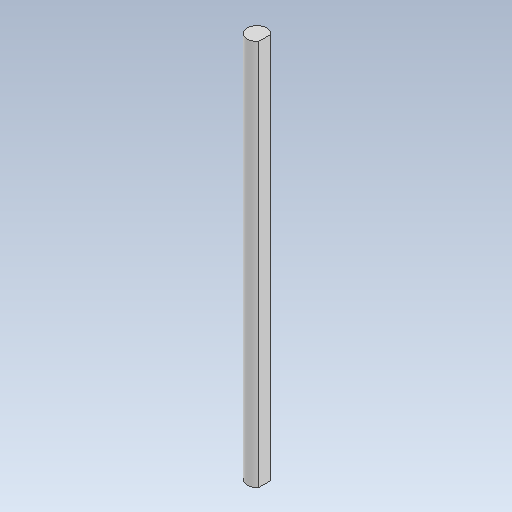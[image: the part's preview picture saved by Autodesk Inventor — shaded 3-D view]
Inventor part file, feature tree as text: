
AUTODESK INVENTOR PART (.ipt)
format: ipt  version: 2020 (Build 240168000, 168)  size: 74,240 bytes
history: native  units: in
note: dims shown in document units (in); Inventor stores cm internally (conversion verified against a paired STEP export)
features: other x3, sketch x1
ambient origin geometry x8: Origin, YZ Plane, XZ Plane, XY Plane, X Axis, Y Axis, Z Axis, Center Point
bodies: Solid1 (feature_tree)
feature tree (4):
  other  "634080.ipt"
  other  "Solid1::634080.ipt"
  other  "TaggingFeature1"
  sketch  "Sketch1"  dims[d0=0.3937in]
